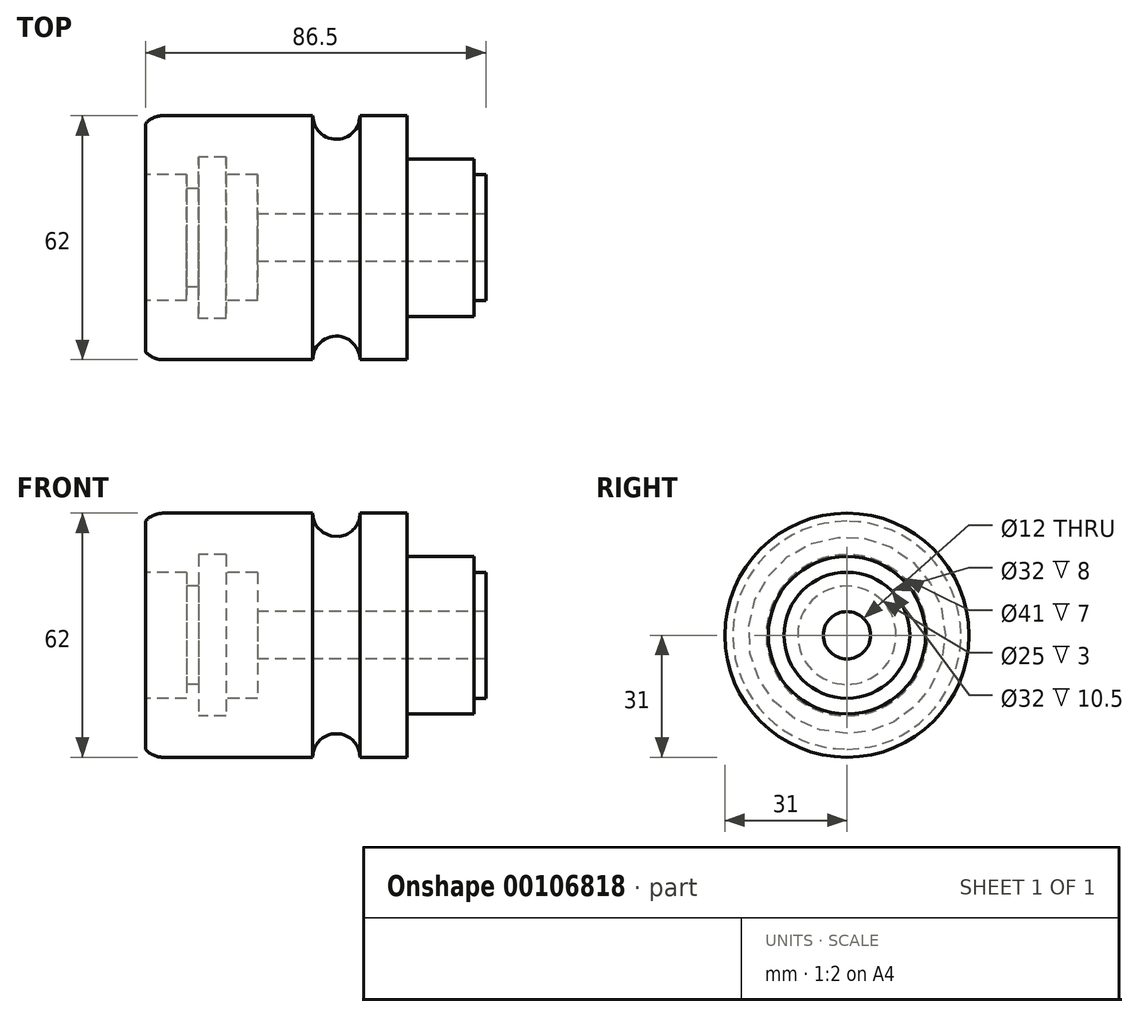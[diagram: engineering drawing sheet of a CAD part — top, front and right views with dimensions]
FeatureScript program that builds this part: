
annotation { "Feature Type Name" : "Feature", "Feature Type Description" : "" }
export const myFeature = defineFeature(function(context is Context, id is Id, definition is map)
    precondition{}
    {
        {
            var Q0;
            Q0=qCreatedBy(makeId("Front.planeOp"),FACE);
            var sketch = newSketch(context, id + "F0", { "sketchPlane" : qUnion([Q0])});
            skLineSegment(sketch, "E0", {"start": v(0, 0) * mm, "end": v(0, 25) * mm});
            skArc(sketch, "E1", {"start": v(6, 31) * mm, "mid": v(1.76, 29.24) * mm, "end": v(0, 25) * mm});
            skLineSegment(sketch, "E2", {"start": v(6, 31) * mm, "end": v(44, 31) * mm});
            skArc(sketch, "E3", {"start": v(44, 31) * mm, "mid": v(50, 25) * mm, "end": v(56, 31) * mm});
            skLineSegment(sketch, "E4", {"start": v(56, 31) * mm, "end": v(68, 31) * mm});
            skLineSegment(sketch, "E5", {"start": v(68, 31) * mm, "end": v(68, 20) * mm});
            skLineSegment(sketch, "E6", {"start": v(68, 20) * mm, "end": v(85, 20) * mm});
            skLineSegment(sketch, "E7", {"start": v(85, 20) * mm, "end": v(85, 0) * mm});
            skLineSegment(sketch, "E8", {"start": v(85, 0) * mm, "end": v(0, 0) * mm});
            skLineSegment(sketch, "E9", {"start": v(44, 31) * mm, "end": v(44, 0) * mm});
            skLineSegment(sketch, "E10", {"start": v(56, 31) * mm, "end": v(56, 0) * mm});
            skLineSegment(sketch, "E11", {"start": v(68, 20) * mm, "end": v(68, 0) * mm});
            skLineSegment(sketch, "E12", {"start": v(85, 16) * mm, "end": v(88, 16) * mm});
            skLineSegment(sketch, "E13", {"start": v(88, 16) * mm, "end": v(88, 0) * mm});
            skLineSegment(sketch, "E14", {"start": v(88, 0) * mm, "end": v(0, 0) * mm});
            skLineSegment(sketch, "E15", {"start": v(44, 31) * mm, "end": v(56, 31) * mm, "construction": true});
            skSolve(sketch);
        }
        {
            var Q0;
            Q0=makeQuery(id+"F0.imprint","IMPRINT",FACE,{"disambiguationData":[TD([[makeQuery(id+"F0.imprint","IMPRINT",EDGE,{"derivedFrom":sQuery(id+"F0.wireOp",EDGE,"E4")}),-1.0]])]});
            var Q1;
            {var subQ3=sQuery(id+"F0.wireOp",EDGE,"E12");Q1=makeQuery(id+"F0.imprint","IMPRINT",FACE,{"disambiguationData":[TD([[makeQuery(id+"F0.imprint","IMPRINT",EDGE,{"derivedFrom":subQ3}),-1.0]])]});}
            var Q2;
            Q2=makeQuery(id+"F0.imprint","IMPRINT",FACE,{"disambiguationData":[TD([[makeQuery(id+"F0.imprint","IMPRINT",EDGE,{"derivedFrom":sQuery(id+"F0.wireOp",EDGE,"E3")}),-1.0]])]});
            var Q3;
            {var subQ1=sQuery(id+"F0.wireOp",EDGE,"E0");Q3=makeQuery(id+"F0.imprint","IMPRINT",FACE,{"disambiguationData":[TD([[makeQuery(id+"F0.imprint","IMPRINT",EDGE,{"derivedFrom":subQ1}),-1.0]])]});}
            var Q4;
            {var subQ5=sQuery(id+"F0.wireOp",EDGE,"E6");Q4=makeQuery(id+"F0.imprint","IMPRINT",FACE,{"disambiguationData":[TD([[makeQuery(id+"F0.imprint","IMPRINT",EDGE,{"derivedFrom":subQ5}),-1.0]])]});}
            var Q5;
            Q5=sQuery(id+"F0.wireOp",EDGE,"E8");
            revolve(context, id + "F1", {"entities" : qUnion([Q0, Q1, Q2, Q3, Q4]), "axis" : qUnion([Q5]), "revolveType" : RevolveType.FULL});
        }
        {
            var Q0;
            Q0=qCreatedBy(makeId("Front.planeOp"),FACE);
            var sketch = newSketch(context, id + "F2", { "sketchPlane" : qUnion([Q0])});
            skLineSegment(sketch, "E16", {"start": v(1.5, 0) * mm, "end": v(1.5, 28.97) * mm});
            skLineSegment(sketch, "E17", {"start": v(1.5, 16) * mm, "end": v(12, 16) * mm});
            skLineSegment(sketch, "E18", {"start": v(12, 16) * mm, "end": v(12, 0) * mm});
            skLineSegment(sketch, "E19", {"start": v(12, 12.5) * mm, "end": v(15, 12.5) * mm});
            skLineSegment(sketch, "E20", {"start": v(15, 12.5) * mm, "end": v(15, 0) * mm});
            skLineSegment(sketch, "E21", {"start": v(15, 12.5) * mm, "end": v(15, 20.5) * mm});
            skLineSegment(sketch, "E22", {"start": v(15, 20.5) * mm, "end": v(22, 20.5) * mm});
            skLineSegment(sketch, "E23", {"start": v(22, 20.5) * mm, "end": v(22, 16) * mm});
            skLineSegment(sketch, "E24", {"start": v(22, 16) * mm, "end": v(30, 16) * mm});
            skLineSegment(sketch, "E25", {"start": v(30, 16) * mm, "end": v(30, 0) * mm});
            skLineSegment(sketch, "E26", {"start": v(30, 6) * mm, "end": v(88, 6) * mm});
            skLineSegment(sketch, "E27", {"start": v(6.75, 16) * mm, "end": v(6.75, 0) * mm, "construction": true});
            skLineSegment(sketch, "E28", {"start": v(18.5, 20.5) * mm, "end": v(18.5, 0) * mm, "construction": true});
            skLineSegment(sketch, "E29", {"start": v(26, 16) * mm, "end": v(26, 0) * mm, "construction": true});
            skLineSegment(sketch, "E30", {"start": v(88, 6) * mm, "end": v(88, 0) * mm});
            skLineSegment(sketch, "E31", {"start": v(88, 0) * mm, "end": v(0, 0) * mm});
            skLineSegment(sketch, "E32", {"start": v(0, 0) * mm, "end": v(0, 16) * mm});
            skLineSegment(sketch, "E33", {"start": v(0, 16) * mm, "end": v(1.5, 16) * mm});
            skLineSegment(sketch, "E34", {"start": v(0, 16) * mm, "end": v(0, 25) * mm});
            skArc(sketch, "E35", {"start": v(1.5, 28.97) * mm, "mid": v(0.39, 27.12) * mm, "end": v(0, 25) * mm});
            skSolve(sketch);
        }
        {
            var Q0;
            Q0 = qSketchRegion(id + "F2", true);
            var Q1;
            Q1=sQuery(id+"F2.wireOp",EDGE,"E31");
            revolve(context, id + "F3", {"operationType" : NewBodyOperationType.REMOVE, "entities" : qUnion([Q0]), "axis" : qUnion([Q1]), "revolveType" : RevolveType.FULL, "oppositeDirection" : true});
        }
    });
